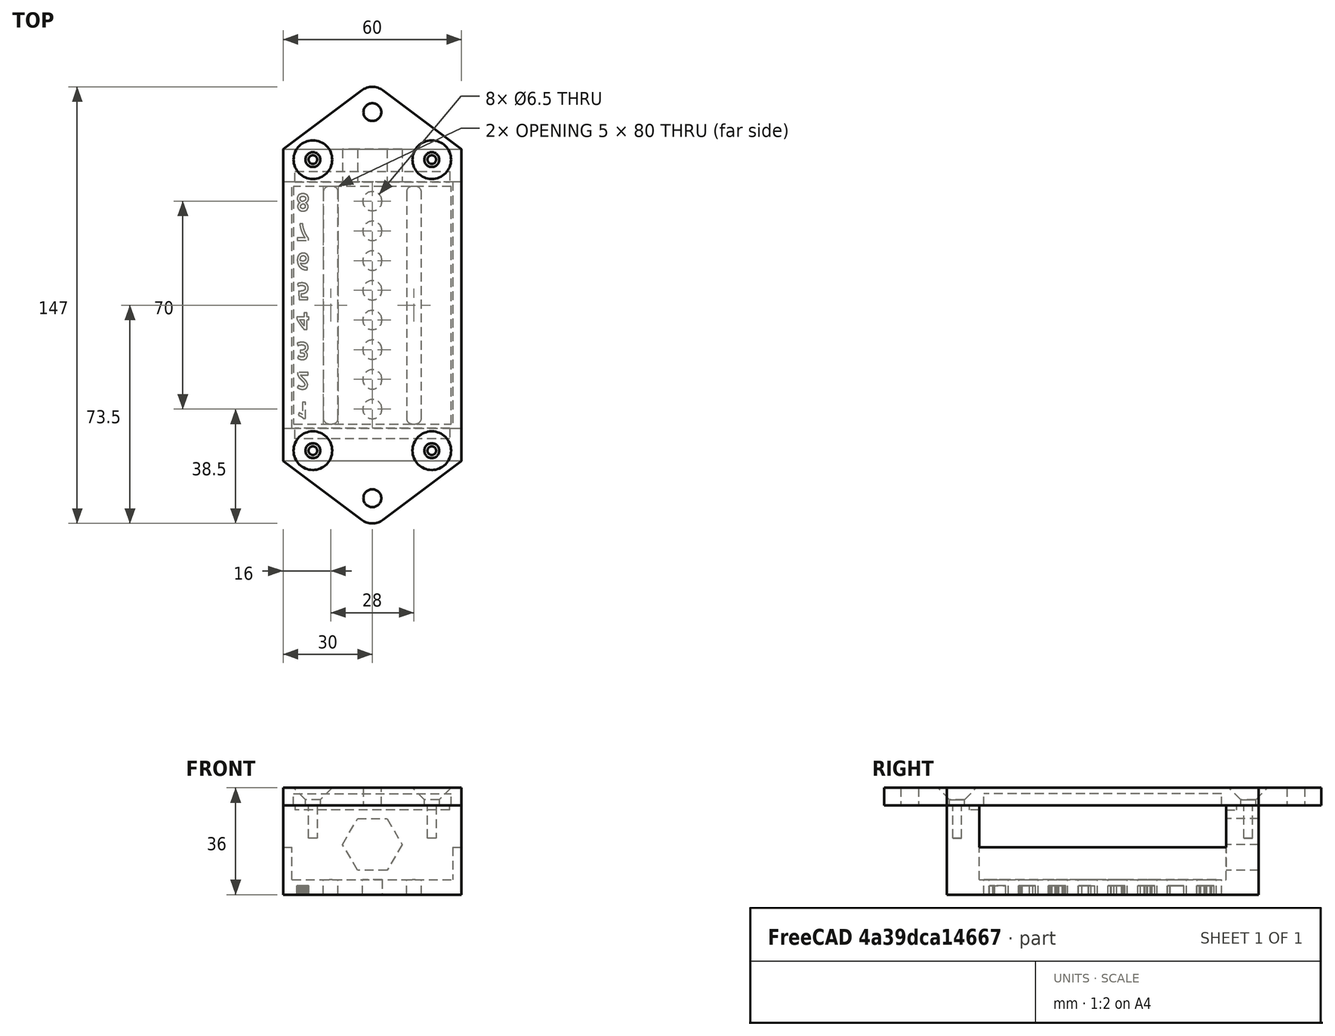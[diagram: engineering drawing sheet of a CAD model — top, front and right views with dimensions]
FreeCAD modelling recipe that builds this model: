
FCSTD DOCUMENT  (FreeCAD 0.19R)
Label: SprinklerSwitch
License: All rights reserved
LicenseURL: http://en.wikipedia.org/wiki/All_rights_reserved
objects: PartDesign::Pocket×17, Sketcher::SketchObject×13, Part::Part2DObjectPython×8, PartDesign::Pad×4, PartDesign::Fillet×2, PartDesign::Body×2, PartDesign::Chamfer×1, Mesh::Feature×1
note: 71 computed .brp shape members not serialized (recipe doc carries the construction recipe); baked Part::Feature solids carry a one-line shape summary decoded from their .brp

FEATURE [Sketcher::SketchObject] Sketch
  FullyConstrained = true
  MapMode = 5
  Support = -> [XY_Plane]
  sketch-geometry (4):
    g0: LineSegment StartX=-30 StartY=52.5 StartZ=0 EndX=30 EndY=52.5 EndZ=0
    g1: LineSegment StartX=30 StartY=52.5 StartZ=0 EndX=30 EndY=-52.5 EndZ=0
    g2: LineSegment StartX=30 StartY=-52.5 StartZ=0 EndX=-30 EndY=-52.5 EndZ=0
    g3: LineSegment StartX=-30 StartY=-52.5 StartZ=0 EndX=-30 EndY=52.5 EndZ=0
  constraints (11):
    c: Coincident(g0,g1)
    c: Coincident(g1,g2)
    c: Coincident(g2,g3)
    c: Coincident(g3,g0)
    c: Horizontal(g0)
    c: Horizontal(g2)
    c: Vertical(g1)
    c: Vertical(g3)
    c: Symmetric(g1,g0,g-1)
    c: Distance(g0) = 60
    c: Distance(g1) = 105
FEATURE [PartDesign::Pad] Pad
  Direction = (1,1,1)
  Length = 5
  Length2 = 100
  Profile = -> Sketch
  Type = 0
FEATURE [Sketcher::SketchObject] Sketch001
  FullyConstrained = true
  MapMode = 5
  Placement = pos=(0,0,5) rot=(0,0,1;0rad)
  Support = -> [Pad]
  sketch-geometry (8):
    g0: Circle CenterX=0 CenterY=35 CenterZ=0 NormalX=0 NormalY=0 NormalZ=1 AngleXU=0 Radius=3.25
    g1: Circle CenterX=0 CenterY=25 CenterZ=0 NormalX=0 NormalY=0 NormalZ=1 AngleXU=0 Radius=3.25
    g2: Circle CenterX=0 CenterY=15 CenterZ=0 NormalX=0 NormalY=0 NormalZ=1 AngleXU=0 Radius=3.25
    g3: Circle CenterX=0 CenterY=5 CenterZ=0 NormalX=0 NormalY=0 NormalZ=1 AngleXU=0 Radius=3.25
    g4: Circle CenterX=0 CenterY=-5 CenterZ=0 NormalX=0 NormalY=0 NormalZ=1 AngleXU=0 Radius=3.25
    g5: Circle CenterX=0 CenterY=-15 CenterZ=0 NormalX=0 NormalY=0 NormalZ=1 AngleXU=0 Radius=3.25
    g6: Circle CenterX=0 CenterY=-25 CenterZ=0 NormalX=0 NormalY=0 NormalZ=1 AngleXU=0 Radius=3.25
    g7: Circle CenterX=0 CenterY=-35 CenterZ=0 NormalX=0 NormalY=0 NormalZ=1 AngleXU=0 Radius=3.25
  constraints (23):
    c: PointOnObject(g0,g-2)
    c: PointOnObject(g1,g-2)
    c: PointOnObject(g2,g-2)
    c: PointOnObject(g3,g-2)
    c: PointOnObject(g4,g-2)
    c: PointOnObject(g5,g-2)
    c: PointOnObject(g6,g-2)
    c: Diameter(g7) = 6.5
    c: Equal(g7,g6)
    c: Equal(g7,g5)
    c: Equal(g7,g4)
    c: Equal(g7,g3)
    c: Equal(g7,g2)
    c: Equal(g7,g1)
    c: Equal(g7,g0)
    c: Distance(g1,g0) = 10
    c: Distance(g2,g1) = 10
    c: Distance(g3,g2) = 10
    c: Distance(g4,g3) = 10
    c: Distance(g5,g4) = 10
    c: Distance(g6,g5) = 10
    c: Distance(g7,g6) = 10
    c: Symmetric(g7,g0,g-1)
FEATURE [PartDesign::Pocket] Pocket
  BaseFeature = -> Pad
  Length = 5
  Length2 = 100
  Profile = -> Sketch001
  Type = 0
FEATURE [Sketcher::SketchObject] Sketch004
  FullyConstrained = true
  MapMode = 5
  Support = -> [XY_Plane001]
  sketch-geometry (6):
    g0: LineSegment StartX=-30 StartY=52.5 StartZ=0 EndX=-30 EndY=-52.5 EndZ=0
    g1: LineSegment StartX=-30 StartY=-52.5 StartZ=0 EndX=0 EndY=-75 EndZ=0
    g2: LineSegment StartX=0 StartY=-75 StartZ=0 EndX=30 EndY=-52.5 EndZ=0
    g3: LineSegment StartX=30 StartY=-52.5 StartZ=0 EndX=30 EndY=52.5 EndZ=0
    g4: LineSegment StartX=30 StartY=52.5 StartZ=0 EndX=0 EndY=75 EndZ=0
    g5: LineSegment StartX=0 StartY=75 StartZ=0 EndX=-30 EndY=52.5 EndZ=0
  constraints (15):
    c: Vertical(g0)
    c: Coincident(g0,g1)
    c: PointOnObject(g1,g-2)
    c: Coincident(g1,g2)
    c: Coincident(g2,g3)
    c: Coincident(g3,g4)
    c: Coincident(g4,g5)
    c: Coincident(g5,g0)
    c: Symmetric(g0,g2,g-1)
    c: Distance(g3) = 105
    c: Distance(g3,g0) = 60
    c: Equal(g3,g0)
    c: Symmetric(g2,g3,g-1)
    c: Symmetric(g1,g4,g-1)
    c: Distance(g1,g4) = 150
FEATURE [Sketcher::SketchObject] Sketch008
  FullyConstrained = true
  MapMode = 5
  Placement = pos=(0,0,5) rot=(0,0,1;0rad)
  Support = -> [Pocket]
  sketch-geometry (8):
    g0: LineSegment StartX=-30 StartY=52.5 StartZ=0 EndX=30 EndY=52.5 EndZ=0
    g1: LineSegment StartX=30 StartY=52.5 StartZ=0 EndX=30 EndY=41.5 EndZ=0
    g2: LineSegment StartX=30 StartY=41.5 StartZ=0 EndX=-30 EndY=41.5 EndZ=0
    g3: LineSegment StartX=-30 StartY=41.5 StartZ=0 EndX=-30 EndY=52.5 EndZ=0
    g4: LineSegment StartX=-30 StartY=-41.5 StartZ=0 EndX=30 EndY=-41.5 EndZ=0
    g5: LineSegment StartX=30 StartY=-41.5 StartZ=0 EndX=30 EndY=-52.5 EndZ=0
    g6: LineSegment StartX=30 StartY=-52.5 StartZ=0 EndX=-30 EndY=-52.5 EndZ=0
    g7: LineSegment StartX=-30 StartY=-52.5 StartZ=0 EndX=-30 EndY=-41.5 EndZ=0
  constraints (21):
    c: Coincident(g0,g1)
    c: Coincident(g1,g2)
    c: Coincident(g2,g3)
    c: Coincident(g3,g0)
    c: Horizontal(g2)
    c: Vertical(g1)
    c: Vertical(g3)
    c: Coincident(g4,g5)
    c: Coincident(g5,g6)
    c: Coincident(g6,g7)
    c: Coincident(g7,g4)
    c: Horizontal(g4)
    c: Horizontal(g6)
    c: Vertical(g7)
    c: Symmetric(g1,g4,g-1)
    c: Distance(g1,g4) = 83
    c: Distance(g5,g0) = 105
    c: Distance(g4) = 60
    c: Symmetric(g0,g0,g-2)
    c: Distance(g0) = 60
    c: Symmetric(g0,g5,g-1)
FEATURE [PartDesign::Pad] Pad004
  BaseFeature = -> Pocket
  Direction = (1,1,1)
  Length = 25
  Length2 = 100
  Profile = -> Sketch008
  Type = 0
FEATURE [Sketcher::SketchObject] Sketch009
  FullyConstrained = true
  MapMode = 5
  Placement = pos=(0,0,30) rot=(0,0,1;0rad)
  Support = -> [Pad004]
  sketch-geometry (4):
    g0: LineSegment StartX=-26 StartY=45 StartZ=0 EndX=26 EndY=45 EndZ=0
    g1: LineSegment StartX=26 StartY=45 StartZ=0 EndX=26 EndY=-45 EndZ=0
    g2: LineSegment StartX=26 StartY=-45 StartZ=0 EndX=-26 EndY=-45 EndZ=0
    g3: LineSegment StartX=-26 StartY=-45 StartZ=0 EndX=-26 EndY=45 EndZ=0
  constraints (10):
    c: Coincident(g0,g1)
    c: Coincident(g1,g2)
    c: Coincident(g2,g3)
    c: Coincident(g3,g0)
    c: Horizontal(g2)
    c: Vertical(g3)
    c: Symmetric(g1,g0,g-1)
    c: Distance(g1) = 90
    c: Distance(g0) = 52
    c: Symmetric(g0,g0,g-2)
FEATURE [PartDesign::Pocket] Pocket004
  BaseFeature = -> Pad004
  Length = 1.5
  Length2 = 100
  Profile = -> Sketch009
  Type = 0
FEATURE [Sketcher::SketchObject] Sketch010
  FullyConstrained = true
  MapMode = 5
  Placement = pos=(0,0,0) rot=(1,0,0;3.14159rad)
  Support = -> [Pocket004]
  sketch-geometry (8):
    g0: LineSegment StartX=11.5 StartY=40 StartZ=0 EndX=16.5 EndY=40 EndZ=0
    g1: LineSegment StartX=16.5 StartY=40 StartZ=0 EndX=16.5 EndY=-40 EndZ=0
    g2: LineSegment StartX=16.5 StartY=-40 StartZ=0 EndX=11.5 EndY=-40 EndZ=0
    g3: LineSegment StartX=11.5 StartY=-40 StartZ=0 EndX=11.5 EndY=40 EndZ=0
    g4: LineSegment StartX=-16.5 StartY=40 StartZ=0 EndX=-11.5 EndY=40 EndZ=0
    g5: LineSegment StartX=-11.5 StartY=40 StartZ=0 EndX=-11.5 EndY=-40 EndZ=0
    g6: LineSegment StartX=-11.5 StartY=-40 StartZ=0 EndX=-16.5 EndY=-40 EndZ=0
    g7: LineSegment StartX=-16.5 StartY=-40 StartZ=0 EndX=-16.5 EndY=40 EndZ=0
  constraints (22):
    c: Coincident(g0,g1)
    c: Coincident(g1,g2)
    c: Coincident(g2,g3)
    c: Coincident(g3,g0)
    c: Horizontal(g0)
    c: Horizontal(g2)
    c: Vertical(g1)
    c: Vertical(g3)
    c: Coincident(g4,g5)
    c: Coincident(g5,g6)
    c: Coincident(g6,g7)
    c: Coincident(g7,g4)
    c: Horizontal(g4)
    c: Horizontal(g6)
    c: Vertical(g5)
    c: Equal(g0,g4)
    c: Distance(g0) = 5
    c: Symmetric(g4,g0,g-2)
    c: Distance(g0,g4) = 28
    c: Symmetric(g4,g6,g-1)
    c: Equal(g3,g5)
    c: Distance(g1) = 80
FEATURE [PartDesign::Pocket] Pocket005
  BaseFeature = -> Pocket004
  Length = 5
  Length2 = 100
  Profile = -> Sketch010
  Type = 0
FEATURE [Sketcher::SketchObject] Sketch011
  FullyConstrained = false
  MapMode = 5
  Placement = pos=(0,52.5,0) rot=(0,0.707107,0.707107;3.14159rad)
  Support = -> [Pocket005]
  sketch-geometry (7):
    g0: LineSegment StartX=5 StartY=8.23171 StartZ=0 EndX=10 EndY=16.892 EndZ=0
    g1: LineSegment StartX=10 StartY=16.892 StartZ=0 EndX=5 EndY=25.5522 EndZ=0
    g2: LineSegment StartX=5 StartY=25.5522 StartZ=0 EndX=-5 EndY=25.5522 EndZ=0
    g3: LineSegment StartX=-5 StartY=25.5522 StartZ=0 EndX=-10 EndY=16.892 EndZ=0
    g4: LineSegment StartX=-10 StartY=16.892 StartZ=0 EndX=-5 EndY=8.23171 EndZ=0
    g5: LineSegment StartX=-5 StartY=8.23171 StartZ=0 EndX=5 EndY=8.23171 EndZ=0
    g6: Circle CenterX=0 CenterY=16.892 CenterZ=0 NormalX=0 NormalY=0 NormalZ=1 AngleXU=0 Radius=10
  constraints (16):
    c: Coincident(g0,g1)
    c: Coincident(g1,g2)
    c: Coincident(g2,g3)
    c: Coincident(g3,g4)
    c: Coincident(g4,g5)
    c: Coincident(g5,g0)
    c: Equal(g0, g1-g5) x5
    c: PointOnObject(g0,g6)
    c: PointOnObject(g1,g6)
    c: PointOnObject(g2,g6)
    c: PointOnObject(g3,g6)
    c: PointOnObject(g4,g6)
    c: PointOnObject(g5,g6)
    c: PointOnObject(g6,g-2)
    c: Diameter(g6) = 20
    c: Horizontal(g2)
FEATURE [PartDesign::Pocket] Pocket006
  BaseFeature = -> Pocket005
  Length = 23
  Length2 = 100
  Profile = -> Sketch011
  Type = 0
FEATURE [PartDesign::Pad] Pad002
  Direction = (1,1,1)
  Length = 6
  Length2 = 100
  Profile = -> Sketch004
  Type = 0
FEATURE [Sketcher::SketchObject] Sketch012
  FullyConstrained = true
  MapMode = 5
  Placement = pos=(0,0,0) rot=(1,0,0;3.14159rad)
  Support = -> [Pad002]
  sketch-geometry (2):
    g0: Circle CenterX=0 CenterY=65 CenterZ=0 NormalX=0 NormalY=0 NormalZ=1 AngleXU=0 Radius=3
    g1: Circle CenterX=0 CenterY=-65 CenterZ=0 NormalX=0 NormalY=0 NormalZ=1 AngleXU=0 Radius=3
  constraints (5):
    c: PointOnObject(g0,g-2)
    c: Symmetric(g1,g0,g-1)
    c: Diameter(g1) = 6
    c: Equal(g1,g0)
    c: DistanceY(g0) = 65
FEATURE [PartDesign::Pocket] Pocket007
  BaseFeature = -> Pad002
  Length = 9
  Length2 = 100
  Profile = -> Sketch012
  Type = 0
FEATURE [Sketcher::SketchObject] Sketch013
  FullyConstrained = true
  MapMode = 5
  Placement = pos=(0,0,0) rot=(1,0,0;3.14159rad)
  Support = -> [Pocket007]
  sketch-geometry (4):
    g0: LineSegment StartX=-26.5 StartY=40 StartZ=0 EndX=26.5 EndY=40 EndZ=0
    g1: LineSegment StartX=26.5 StartY=40 StartZ=0 EndX=26.5 EndY=-40 EndZ=0
    g2: LineSegment StartX=26.5 StartY=-40 StartZ=0 EndX=-26.5 EndY=-40 EndZ=0
    g3: LineSegment StartX=-26.5 StartY=-40 StartZ=0 EndX=-26.5 EndY=40 EndZ=0
  constraints (10):
    c: Coincident(g0,g1)
    c: Coincident(g1,g2)
    c: Coincident(g2,g3)
    c: Coincident(g3,g0)
    c: Horizontal(g2)
    c: Vertical(g3)
    c: Symmetric(g1,g0,g-1)
    c: Distance(g1) = 80
    c: Distance(g0) = 53
    c: Symmetric(g0,g0,g-2)
FEATURE [PartDesign::Pocket] Pocket008
  BaseFeature = -> Pocket007
  Length = 4
  Length2 = 100
  Profile = -> Sketch013
  Type = 0
FEATURE [Sketcher::SketchObject] Sketch014
  FullyConstrained = true
  MapMode = 5
  Placement = pos=(0,0,6) rot=(0,0,1;0rad)
  Support = -> [Pocket008]
  sketch-geometry (8):
    g0: Circle CenterX=-20 CenterY=49 CenterZ=0 NormalX=0 NormalY=0 NormalZ=1 AngleXU=0 Radius=2.5
    g1: Circle CenterX=20 CenterY=49 CenterZ=0 NormalX=0 NormalY=0 NormalZ=1 AngleXU=0 Radius=2.5
    g2: Circle CenterX=-20 CenterY=-49 CenterZ=0 NormalX=0 NormalY=0 NormalZ=1 AngleXU=0 Radius=2.5
    g3: Circle CenterX=20 CenterY=-49 CenterZ=0 NormalX=0 NormalY=0 NormalZ=1 AngleXU=0 Radius=2.5
    g4: LineSegment StartX=-20 StartY=49 StartZ=0 EndX=20 EndY=49 EndZ=0
    g5: LineSegment StartX=20 StartY=49 StartZ=0 EndX=20 EndY=-49 EndZ=0
    g6: LineSegment StartX=20 StartY=-49 StartZ=0 EndX=-20 EndY=-49 EndZ=0
    g7: LineSegment StartX=-20 StartY=-49 StartZ=0 EndX=-20 EndY=49 EndZ=0
  constraints (18):
    c: Coincident(g4,g5)
    c: Coincident(g5,g6)
    c: Coincident(g6,g7)
    c: Coincident(g7,g4)
    c: Horizontal(g6)
    c: Vertical(g7)
    c: Coincident(g4,g0)
    c: Coincident(g5,g3)
    c: Coincident(g1,g4)
    c: Coincident(g6,g2)
    c: Distance(g4) = 40
    c: Distance(g5) = 98
    c: Diameter(g0) = 5
    c: Equal(g0,g1)
    c: Equal(g0,g3)
    c: Equal(g0,g2)
    c: Symmetric(g1,g0,g-2)
    c: Symmetric(g3,g1,g-1)
FEATURE [PartDesign::Pocket] Pocket009
  BaseFeature = -> Pocket008
  Length = 5
  Length2 = 100
  Profile = -> Sketch014
  Type = 1
FEATURE [Sketcher::SketchObject] Sketch015
  FullyConstrained = false
  MapMode = 5
  Placement = pos=(-0.185566,0,-0.107137) rot=(0.447214,0.447214,0.774597;1.82348rad)
  Support = -> [Pocket006]
  sketch-geometry (8):
    g0: LineSegment StartX=-20 StartY=49 StartZ=0 EndX=20 EndY=49 EndZ=0
    g1: LineSegment StartX=20 StartY=49 StartZ=0 EndX=20 EndY=-49 EndZ=0
    g2: LineSegment StartX=20 StartY=-49 StartZ=0 EndX=-20 EndY=-49 EndZ=0
    g3: LineSegment StartX=-20 StartY=-49 StartZ=0 EndX=-20 EndY=49 EndZ=0
    g4: Circle CenterX=-20 CenterY=-49 CenterZ=0 NormalX=0 NormalY=0 NormalZ=1 AngleXU=0 Radius=1.4
    g5: Circle CenterX=20 CenterY=-49 CenterZ=0 NormalX=0 NormalY=0 NormalZ=1 AngleXU=0 Radius=1.4
    g6: Circle CenterX=20 CenterY=49 CenterZ=0 NormalX=0 NormalY=0 NormalZ=1 AngleXU=0 Radius=1.4
    g7: Circle CenterX=-20 CenterY=49 CenterZ=0 NormalX=0 NormalY=0 NormalZ=1 AngleXU=0 Radius=1.4
  constraints (16):
    c: Coincident(g0,g1)
    c: Coincident(g1,g2)
    c: Coincident(g2,g3)
    c: Coincident(g3,g0)
    c: Horizontal(g2)
    c: Vertical(g3)
    c: Coincident(g4,g2)
    c: Coincident(g5,g1)
    c: Coincident(g6,g0)
    c: Diameter(g7) = 2.8
    c: Equal(g7,g6)
    c: Equal(g7,g5)
    c: Equal(g7,g4)
    c: Symmetric(g6,g5,g-1)
    c: Distance(g2) = 40
    c: Distance(g1) = 98
FEATURE [PartDesign::Pocket] Pocket010
  BaseFeature = -> Pocket006
  Length = 10
  Length2 = 100
  Profile = -> Sketch015
  Type = 0
FEATURE [PartDesign::Chamfer] Chamfer
  Angle = 45
  Base = -> Pocket009 [Edge32,Edge30,Edge29,Edge27]
  BaseFeature = -> Pocket009
  ChamferType = 0
  FlipDirection = false
  Size = 4
  Size2 = 1
  SupportTransform = false
FEATURE [PartDesign::Fillet] Fillet
  Base = -> Chamfer [Edge18,Edge20]
  BaseFeature = -> Chamfer
  Radius = 6
  SupportTransform = false
FEATURE [PartDesign::Body] Body001
  Group = -> [Sketch004,Pad002,Sketch012,Pocket007,Sketch013,Pocket008,Sketch014,Pocket009,Chamfer,Fillet]
  Origin = -> Origin001
  Placement = pos=(0,0,30) rot=(0,0,1;0rad)
  Tip = -> Fillet
FEATURE [Part::Part2DObjectPython] ShapeString  # Draft 2D object (typed FeaturePython)
  FontFile = <path>
  Placement = pos=(-25.64,-32.65,0) rot=(1,0,0;3.14159rad)
  Size = 3
  String = 1
  Tracking = 0
FEATURE [Part::Part2DObjectPython] ShapeString001  # Draft 2D object (typed FeaturePython)
  FontFile = <path>
  Placement = pos=(-25.64,-22.65,0) rot=(1,0,0;3.14159rad)
  Size = 3
  String = 2
  Tracking = 0
FEATURE [Part::Part2DObjectPython] ShapeString002  # Draft 2D object (typed FeaturePython)
  FontFile = <path>
  Placement = pos=(-25.64,-12.65,0) rot=(1,0,0;3.14159rad)
  Size = 3
  String = 3
  Tracking = 0
FEATURE [Part::Part2DObjectPython] ShapeString003  # Draft 2D object (typed FeaturePython)
  FontFile = <path>
  Placement = pos=(-25.64,-2.65,0) rot=(1,0,0;3.14159rad)
  Size = 3
  String = 4
  Tracking = 0
FEATURE [Part::Part2DObjectPython] ShapeString004  # Draft 2D object (typed FeaturePython)
  FontFile = <path>
  Placement = pos=(-25.64,7.35,0) rot=(1,0,0;3.14159rad)
  Size = 3
  String = 5
  Tracking = 0
FEATURE [Part::Part2DObjectPython] ShapeString005  # Draft 2D object (typed FeaturePython)
  FontFile = <path>
  Placement = pos=(-25.64,17.35,0) rot=(1,0,0;3.14159rad)
  Size = 3
  String = 6
  Tracking = 0
FEATURE [Part::Part2DObjectPython] ShapeString006  # Draft 2D object (typed FeaturePython)
  FontFile = <path>
  Placement = pos=(-25.64,27.35,0) rot=(1,0,0;3.14159rad)
  Size = 3
  String = 7
  Tracking = 0
FEATURE [Part::Part2DObjectPython] ShapeString007  # Draft 2D object (typed FeaturePython)
  FontFile = <path>
  Placement = pos=(-25.64,37.35,0) rot=(1,0,0;3.14159rad)
  Size = 3
  String = 8
  Tracking = 0
FEATURE [PartDesign::Pocket] Pocket011
  BaseFeature = -> Pocket010
  Length = 3
  Length2 = 100
  Profile = -> ShapeString
  Type = 0
FEATURE [PartDesign::Pocket] Pocket012
  BaseFeature = -> Pocket011
  Length = 3
  Length2 = 100
  Profile = -> ShapeString001
  Type = 0
FEATURE [PartDesign::Pocket] Pocket013
  BaseFeature = -> Pocket012
  Length = 3
  Length2 = 100
  Profile = -> ShapeString004
  Type = 0
FEATURE [PartDesign::Pocket] Pocket014
  BaseFeature = -> Pocket013
  Length = 3
  Length2 = 100
  Profile = -> ShapeString002
  Type = 0
FEATURE [PartDesign::Pocket] Pocket015
  BaseFeature = -> Pocket014
  Length = 3
  Length2 = 100
  Profile = -> ShapeString006
  Type = 0
FEATURE [PartDesign::Pocket] Pocket016
  BaseFeature = -> Pocket015
  Length = 3
  Length2 = 100
  Profile = -> ShapeString003
  Type = 0
FEATURE [PartDesign::Pocket] Pocket017
  BaseFeature = -> Pocket016
  Length = 3
  Length2 = 100
  Profile = -> ShapeString007
  Type = 0
FEATURE [PartDesign::Pocket] Pocket018
  BaseFeature = -> Pocket017
  Length = 3
  Length2 = 100
  Profile = -> ShapeString005
  Type = 0
FEATURE [Sketcher::SketchObject] Sketch016
  FullyConstrained = true
  MapMode = 5
  Placement = pos=(0,0,0) rot=(1,0,0;3.14159rad)
  Support = -> [Pocket018]
  sketch-geometry (8):
    g0: LineSegment StartX=-30 StartY=52.5 StartZ=0 EndX=-27 EndY=52.5 EndZ=0
    g1: LineSegment StartX=-27 StartY=52.5 StartZ=0 EndX=-27 EndY=-52.5 EndZ=0
    g2: LineSegment StartX=-27 StartY=-52.5 StartZ=0 EndX=-30 EndY=-52.5 EndZ=0
    g3: LineSegment StartX=-30 StartY=-52.5 StartZ=0 EndX=-30 EndY=52.5 EndZ=0
    g4: LineSegment StartX=27 StartY=52.5 StartZ=0 EndX=30 EndY=52.5 EndZ=0
    g5: LineSegment StartX=30 StartY=52.5 StartZ=0 EndX=30 EndY=-52.5 EndZ=0
    g6: LineSegment StartX=30 StartY=-52.5 StartZ=0 EndX=27 EndY=-52.5 EndZ=0
    g7: LineSegment StartX=27 StartY=-52.5 StartZ=0 EndX=27 EndY=52.5 EndZ=0
  constraints (22):
    c: Coincident(g0,g1)
    c: Coincident(g1,g2)
    c: Coincident(g2,g3)
    c: Coincident(g3,g0)
    c: Horizontal(g0)
    c: Horizontal(g2)
    c: Vertical(g1)
    c: Vertical(g3)
    c: Coincident(g4,g5)
    c: Coincident(g5,g6)
    c: Coincident(g6,g7)
    c: Coincident(g7,g4)
    c: Horizontal(g4)
    c: Horizontal(g6)
    c: Vertical(g7)
    c: Symmetric(g4,g0,g-2)
    c: Distance(g0) = 3
    c: Equal(g4,g0)
    c: Symmetric(g5,g4,g-1)
    c: Distance(g5) = 105
    c: Distance(g0,g4) = 60
    c: Equal(g1,g7)
FEATURE [PartDesign::Pad] Pad005
  BaseFeature = -> Pocket018
  Direction = (1,1,1)
  Length = 16
  Length2 = 100
  Profile = -> Sketch016
  Reversed = true
  Type = 0
FEATURE [PartDesign::Fillet] Fillet001
  Base = -> Pad005 [Edge458,Edge474,Edge460,Edge476,Edge456,Edge472,Edge455,Edge471]
  BaseFeature = -> Pad005
  Radius = 2
  SupportTransform = false
FEATURE [Sketcher::SketchObject] Sketch017
  FullyConstrained = true
  MapMode = 5
  Placement = pos=(0,0,30) rot=(0,0,1;0rad)
  Support = -> [Fillet001]
  sketch-geometry (8):
    g0: LineSegment StartX=-20 StartY=49 StartZ=0 EndX=20 EndY=49 EndZ=0
    g1: LineSegment StartX=20 StartY=49 StartZ=0 EndX=20 EndY=-49 EndZ=0
    g2: LineSegment StartX=20 StartY=-49 StartZ=0 EndX=-20 EndY=-49 EndZ=0
    g3: LineSegment StartX=-20 StartY=-49 StartZ=0 EndX=-20 EndY=49 EndZ=0
    g4: Circle CenterX=-20 CenterY=49 CenterZ=0 NormalX=0 NormalY=0 NormalZ=1 AngleXU=0 Radius=1.45
    g5: Circle CenterX=20 CenterY=49 CenterZ=0 NormalX=0 NormalY=0 NormalZ=1 AngleXU=0 Radius=1.45
    g6: Circle CenterX=20 CenterY=-49 CenterZ=0 NormalX=0 NormalY=0 NormalZ=1 AngleXU=0 Radius=1.45
    g7: Circle CenterX=-20 CenterY=-49 CenterZ=0 NormalX=0 NormalY=0 NormalZ=1 AngleXU=0 Radius=1.45
  constraints (19):
    c: Coincident(g0,g1)
    c: Coincident(g1,g2)
    c: Coincident(g2,g3)
    c: Coincident(g3,g0)
    c: Horizontal(g0)
    c: Horizontal(g2)
    c: Vertical(g1)
    c: Vertical(g3)
    c: Distance(g2) = 40
    c: Distance(g1) = 98
    c: Symmetric(g0,g2,g-1)
    c: Coincident(g4,g0)
    c: Coincident(g5,g0)
    c: Coincident(g6,g1)
    c: Coincident(g7,g2)
    c: Diameter(g7) = 2.9
    c: Equal(g7,g6)
    c: Equal(g7,g5)
    c: Equal(g7,g4)
FEATURE [PartDesign::Pocket] Pocket019
  BaseFeature = -> Fillet001
  Length = 11
  Length2 = 100
  Profile = -> Sketch017
  Type = 0
FEATURE [PartDesign::Body] Body
  Group = -> [Sketch,Pad,Sketch001,Pocket,Sketch008,Pad004,Sketch009,Pocket004,Sketch010,Pocket005,Sketch011,Pocket006,Sketch015,Pocket010,ShapeString,ShapeString001,ShapeString002,ShapeString003,ShapeString004,ShapeString005,ShapeString006,ShapeString007,Pocket011,Pocket012,Pocket013,Pocket014,Pocket015,Pocket016,Pocket017,Pocket018,Sketch016,Pad005,Fillet001,Sketch017,Pocket019]
  Origin = -> Origin
  Tip = -> Pocket019
FEATURE [Mesh::Feature] Mesh  label="Pocket019 (Meshed)"
note: 8 file-system paths scrubbed to <path> (originals preserved in the JSON sidecar)
